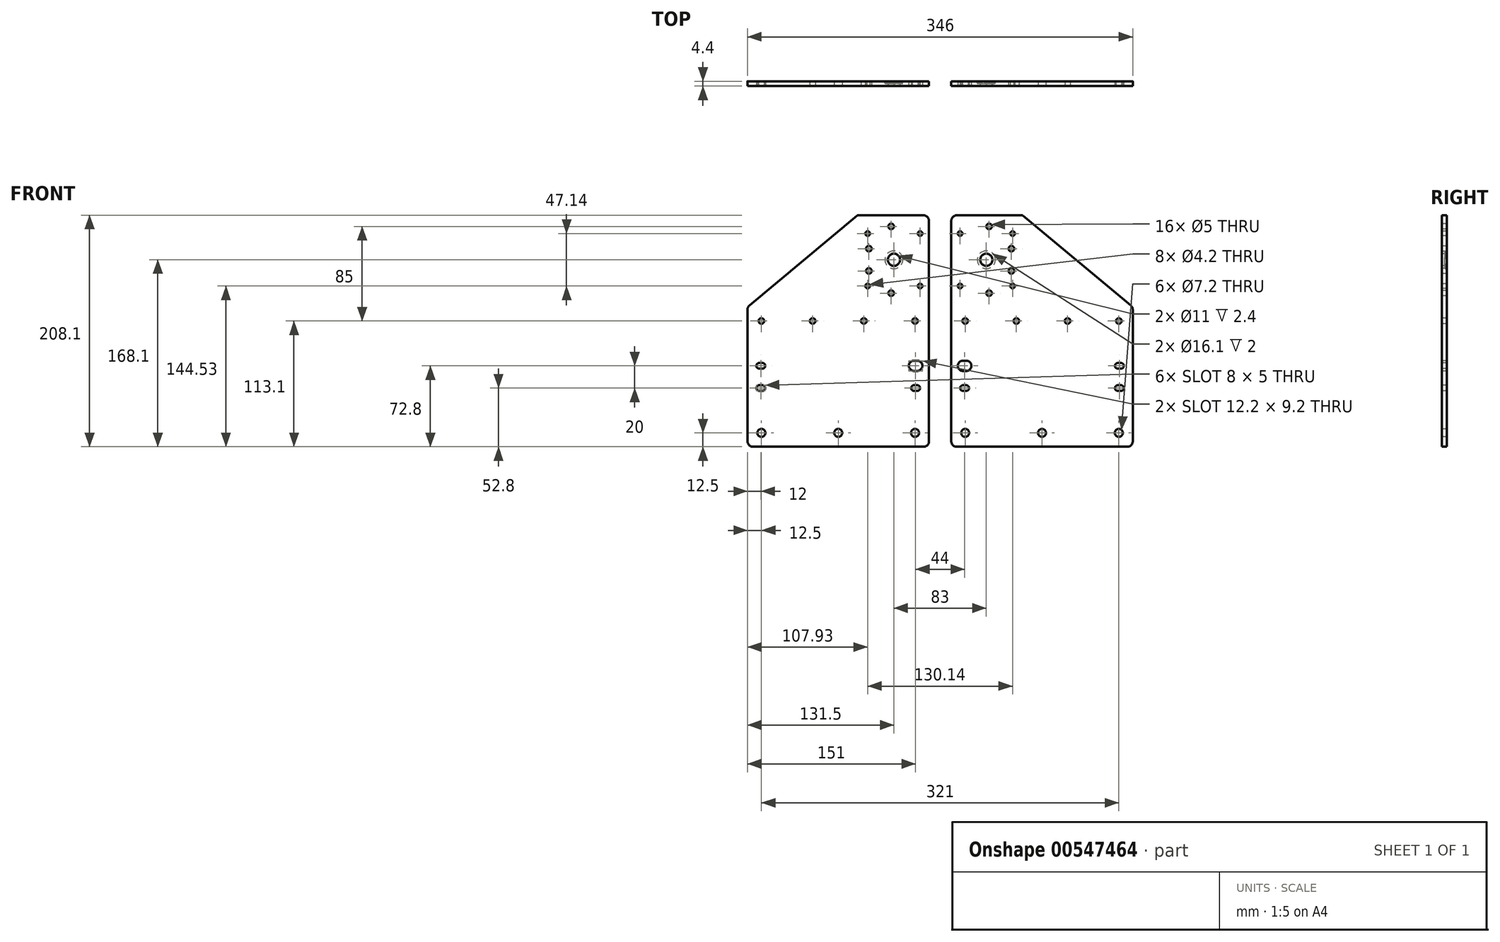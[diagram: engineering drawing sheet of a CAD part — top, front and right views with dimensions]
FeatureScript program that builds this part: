
annotation { "Feature Type Name" : "Feature", "Feature Type Description" : "" }
export const myFeature = defineFeature(function(context is Context, id is Id, definition is map)
    precondition{}
    {
        {
            var Q0;
            Q0=qCreatedBy(makeId("Front.planeOp"),FACE);
            var sketch = newSketch(context, id + "F0", { "sketchPlane" : qUnion([Q0])});
            skCircle(sketch, "E0", {"center": v(-69, -50.3) * mm, "radius": 3.6 * mm});
            skCircle(sketch, "E1", {"center": v(-69, -50.3) * mm, "radius": 6.12 * mm});
            skCircle(sketch, "E2.1.0.0", {"center": v(0, -50.3) * mm, "radius": 6.12 * mm});
            skCircle(sketch, "E2.1.0.1", {"center": v(0, -50.3) * mm, "radius": 3.6 * mm});
            skCircle(sketch, "E2.2.0.0", {"center": v(69, -50.3) * mm, "radius": 6.12 * mm});
            skCircle(sketch, "E2.2.0.1", {"center": v(69, -50.3) * mm, "radius": 3.6 * mm});
            skLineSegment(sketch, "E2.direction1", {"start": v(-69, -50.3) * mm, "end": v(0, -50.3) * mm, "construction": true});
            skArc(sketch, "E3", {"start": v(-68, -12.5) * mm, "mid": v(-65.5, -10) * mm, "end": v(-68, -7.5) * mm});
            skArc(sketch, "E4", {"start": v(-71, -7.5) * mm, "mid": v(-73.5, -10) * mm, "end": v(-71, -12.5) * mm});
            skArc(sketch, "E5", {"start": v(-71, -5.4) * mm, "mid": v(-75.6, -10) * mm, "end": v(-71, -14.6) * mm});
            skArc(sketch, "E6", {"start": v(-68, -14.6) * mm, "mid": v(-63.4, -10) * mm, "end": v(-68, -5.4) * mm});
            skLineSegment(sketch, "E7", {"start": v(-71, -5.4) * mm, "end": v(-68, -5.4) * mm});
            skLineSegment(sketch, "E8", {"start": v(-71, -14.6) * mm, "end": v(-68, -14.6) * mm});
            skLineSegment(sketch, "E9", {"start": v(-71, -12.5) * mm, "end": v(-68, -12.5) * mm});
            skLineSegment(sketch, "E10", {"start": v(-71, -7.5) * mm, "end": v(-68, -7.5) * mm});
            skArc(sketch, "E11.MirrorCS", {"start": v(-71, 5.4) * mm, "mid": v(-75.6, 10) * mm, "end": v(-71, 14.6) * mm});
            skArc(sketch, "E12.MirrorCS", {"start": v(-71, 7.5) * mm, "mid": v(-73.5, 10) * mm, "end": v(-71, 12.5) * mm});
            skArc(sketch, "E13.MirrorCS", {"start": v(-68, 14.6) * mm, "mid": v(-63.4, 10) * mm, "end": v(-68, 5.4) * mm});
            skArc(sketch, "E14.MirrorCS", {"start": v(-68, 12.5) * mm, "mid": v(-65.5, 10) * mm, "end": v(-68, 7.5) * mm});
            skLineSegment(sketch, "E15.MirrorCS", {"start": v(-71, 7.5) * mm, "end": v(-68, 7.5) * mm});
            skLineSegment(sketch, "E16.MirrorCS", {"start": v(-71, 5.4) * mm, "end": v(-68, 5.4) * mm});
            skLineSegment(sketch, "E17.MirrorCS", {"start": v(-71, 12.5) * mm, "end": v(-68, 12.5) * mm});
            skLineSegment(sketch, "E18.MirrorCS", {"start": v(-71, 14.6) * mm, "end": v(-68, 14.6) * mm});
            skLineSegment(sketch, "E19.MirrorCS", {"start": v(71, -12.5) * mm, "end": v(68, -12.5) * mm});
            skLineSegment(sketch, "E20.MirrorCS", {"start": v(71, 7.5) * mm, "end": v(68, 7.5) * mm});
            skLineSegment(sketch, "E21.MirrorCS", {"start": v(71, 14.6) * mm, "end": v(68, 14.6) * mm});
            skLineSegment(sketch, "E22.MirrorCS", {"start": v(71, 12.5) * mm, "end": v(68, 12.5) * mm});
            skLineSegment(sketch, "E23.MirrorCS", {"start": v(71, -5.4) * mm, "end": v(68, -5.4) * mm});
            skLineSegment(sketch, "E24.MirrorCS", {"start": v(71, -14.6) * mm, "end": v(68, -14.6) * mm});
            skLineSegment(sketch, "E25.MirrorCS", {"start": v(71, 5.4) * mm, "end": v(68, 5.4) * mm});
            skLineSegment(sketch, "E26.MirrorCS", {"start": v(71, -7.5) * mm, "end": v(68, -7.5) * mm});
            skArc(sketch, "E27.MirrorCS", {"start": v(71, -7.5) * mm, "mid": v(73.5, -10) * mm, "end": v(71, -12.5) * mm});
            skArc(sketch, "E28.MirrorCS", {"start": v(71, 7.5) * mm, "mid": v(73.5, 10) * mm, "end": v(71, 12.5) * mm});
            skArc(sketch, "E29.MirrorCS", {"start": v(71, 5.4) * mm, "mid": v(75.6, 10) * mm, "end": v(71, 14.6) * mm});
            skArc(sketch, "E30.MirrorCS", {"start": v(68, 14.6) * mm, "mid": v(63.4, 10) * mm, "end": v(68, 5.4) * mm});
            skArc(sketch, "E31.MirrorCS", {"start": v(71, -5.4) * mm, "mid": v(75.6, -10) * mm, "end": v(71, -14.6) * mm});
            skArc(sketch, "E32.MirrorCS", {"start": v(68, -12.5) * mm, "mid": v(65.5, -10) * mm, "end": v(68, -7.5) * mm});
            skArc(sketch, "E33.MirrorCS", {"start": v(68, 12.5) * mm, "mid": v(65.5, 10) * mm, "end": v(68, 7.5) * mm});
            skArc(sketch, "E34.MirrorCS", {"start": v(68, -14.6) * mm, "mid": v(63.4, -10) * mm, "end": v(68, -5.4) * mm});
            skCircle(sketch, "E35", {"center": v(-69, 50.3) * mm, "radius": 2.5 * mm});
            skCircle(sketch, "E36", {"center": v(-69, 50.3) * mm, "radius": 4.6 * mm});
            skCircle(sketch, "E37.1.0.0", {"center": v(-23, 50.3) * mm, "radius": 4.6 * mm});
            skCircle(sketch, "E37.1.0.1", {"center": v(-23, 50.3) * mm, "radius": 2.5 * mm});
            skCircle(sketch, "E37.2.0.0", {"center": v(23, 50.3) * mm, "radius": 4.6 * mm});
            skCircle(sketch, "E37.2.0.1", {"center": v(23, 50.3) * mm, "radius": 2.5 * mm});
            skCircle(sketch, "E37.3.0.0", {"center": v(69, 50.3) * mm, "radius": 4.6 * mm});
            skCircle(sketch, "E37.3.0.1", {"center": v(69, 50.3) * mm, "radius": 2.5 * mm});
            skLineSegment(sketch, "E37.direction1", {"start": v(-69, 50.3) * mm, "end": v(-23, 50.3) * mm, "construction": true});
            skCircle(sketch, "E38", {"center": v(-47.5, 75.3) * mm, "radius": 2.5 * mm});
            skCircle(sketch, "E39", {"center": v(-47.5, 75.3) * mm, "radius": 4.6 * mm});
            skCircle(sketch, "E40", {"center": v(-47.5, 135.3) * mm, "radius": 2.5 * mm});
            skCircle(sketch, "E41", {"center": v(-47.5, 135.3) * mm, "radius": 4.6 * mm});
            skCircle(sketch, "E42", {"center": v(-27.5, 115.3) * mm, "radius": 2.5 * mm});
            skCircle(sketch, "E43", {"center": v(-27.5, 115.3) * mm, "radius": 4.6 * mm});
            skCircle(sketch, "E44", {"center": v(-27.5, 95.3) * mm, "radius": 2.5 * mm});
            skCircle(sketch, "E45", {"center": v(-27.5, 95.3) * mm, "radius": 4.6 * mm});
            skCircle(sketch, "E46", {"center": v(-50, 105.3) * mm, "radius": 5.5 * mm});
            skCircle(sketch, "E47", {"center": v(-73.57, 128.87) * mm, "radius": 2.1 * mm});
            skCircle(sketch, "E48.1.0", {"center": v(-73.57, 81.73) * mm, "radius": 2.1 * mm});
            skCircle(sketch, "E48.2.0", {"center": v(-26.43, 81.73) * mm, "radius": 2.1 * mm});
            skCircle(sketch, "E48.3.0", {"center": v(-26.43, 128.87) * mm, "radius": 2.1 * mm});
            skLineSegment(sketch, "E49.bottom", {"start": v(-57.5, 65.3) * mm, "end": v(-17.5, 65.3) * mm, "construction": true});
            skLineSegment(sketch, "E49.top", {"start": v(-57.5, 145.3) * mm, "end": v(-17.5, 145.3) * mm, "construction": true});
            skLineSegment(sketch, "E49.left", {"start": v(-57.5, 65.3) * mm, "end": v(-57.5, 145.3) * mm, "construction": true});
            skLineSegment(sketch, "E49.right", {"start": v(-17.5, 65.3) * mm, "end": v(-17.5, 145.3) * mm, "construction": true});
            skCircle(sketch, "E50", {"center": v(-69, -50.3) * mm, "radius": 12.5 * mm, "construction": true});
            skCircle(sketch, "E51", {"center": v(69, -50.3) * mm, "radius": 12.5 * mm, "construction": true});
            skCircle(sketch, "E52", {"center": v(69, 50.3) * mm, "radius": 12.5 * mm, "construction": true});
            skLineSegment(sketch, "E53", {"start": v(-76.5, -62.8) * mm, "end": v(76.5, -62.8) * mm});
            skLineSegment(sketch, "E54", {"start": v(81.5, -57.8) * mm, "end": v(81.5, 60.46) * mm});
            skCircle(sketch, "E55", {"center": v(-69, 50.3) * mm, "radius": 12.5 * mm, "construction": true});
            skLineSegment(sketch, "E56", {"start": v(-81.5, -57.8) * mm, "end": v(-81.5, 140.3) * mm});
            skLineSegment(sketch, "E57", {"start": v(-81.5, 62.8) * mm, "end": v(81.5, 62.8) * mm, "construction": true});
            skCircle(sketch, "E58", {"center": v(-47.5, 135.3) * mm, "radius": 10 * mm, "construction": true});
            skLineSegment(sketch, "E59", {"start": v(-76.5, 145.3) * mm, "end": v(-18.04, 145.3) * mm});
            skLineSegment(sketch, "E60", {"start": v(-17.08, 144.95) * mm, "end": v(79.7, 64.3) * mm});
            skPoint(sketch, "E61.visualSharp", {"position": v(-81.5, -62.8) * mm});
            skArc(sketch, "E61.filletArc", {"start": v(-81.5, -57.8) * mm, "mid": v(-80.04, -61.34) * mm, "end": v(-76.5, -62.8) * mm});
            skPoint(sketch, "E62.visualSharp", {"position": v(81.5, -62.8) * mm});
            skArc(sketch, "E62.filletArc", {"start": v(76.5, -62.8) * mm, "mid": v(80.04, -61.34) * mm, "end": v(81.5, -57.8) * mm});
            skPoint(sketch, "E63.visualSharp", {"position": v(-81.5, 145.3) * mm});
            skArc(sketch, "E63.filletArc", {"start": v(-76.5, 145.3) * mm, "mid": v(-80.04, 143.84) * mm, "end": v(-81.5, 140.3) * mm});
            skPoint(sketch, "E64.visualSharp", {"position": v(81.5, 62.8) * mm});
            skArc(sketch, "E64.filletArc", {"start": v(81.5, 60.46) * mm, "mid": v(81.03, 62.58) * mm, "end": v(79.7, 64.3) * mm});
            skPoint(sketch, "E65.visualSharp", {"position": v(-17.5, 145.3) * mm});
            skArc(sketch, "E65.filletArc", {"start": v(-17.08, 144.95) * mm, "mid": v(-17.53, 145.21) * mm, "end": v(-18.04, 145.3) * mm});
            skSolve(sketch);
        }
        {
            var Q0;
            Q0=makeQuery(id+"F0.imprint","IMPRINT",FACE,{"disambiguationData":[TD([[makeQuery(id+"F0.imprint","IMPRINT",EDGE,{"derivedFrom":sQuery(id+"F0.wireOp",EDGE,"E1")}),-1.0]])]});
            var Q1;
            Q1=makeQuery(id+"F0.imprint","IMPRINT",FACE,{"disambiguationData":[TD([[makeQuery(id+"F0.imprint","IMPRINT",EDGE,{"derivedFrom":sQuery(id+"F0.wireOp",EDGE,"E3")}),-1.0]])]});
            var Q2;
            Q2=makeQuery(id+"F0.imprint","IMPRINT",FACE,{"disambiguationData":[TD([[makeQuery(id+"F0.imprint","IMPRINT",EDGE,{"derivedFrom":sQuery(id+"F0.wireOp",EDGE,"E11.MirrorCS")}),-1.0]])]});
            var Q3;
            Q3=makeQuery(id+"F0.imprint","IMPRINT",FACE,{"disambiguationData":[TD([[makeQuery(id+"F0.imprint","IMPRINT",EDGE,{"derivedFrom":sQuery(id+"F0.wireOp",EDGE,"E0")}),-1.0]])]});
            var Q4;
            Q4=makeQuery(id+"F0.imprint","IMPRINT",FACE,{"disambiguationData":[TD([[makeQuery(id+"F0.imprint","IMPRINT",EDGE,{"derivedFrom":sQuery(id+"F0.wireOp",EDGE,"E2.1.0.0")}),1.0]])]});
            var Q5;
            Q5=makeQuery(id+"F0.imprint","IMPRINT",FACE,{"disambiguationData":[TD([[makeQuery(id+"F0.imprint","IMPRINT",EDGE,{"derivedFrom":sQuery(id+"F0.wireOp",EDGE,"E2.2.0.0")}),1.0]])]});
            var Q6;
            Q6=makeQuery(id+"F0.imprint","IMPRINT",FACE,{"disambiguationData":[TD([[makeQuery(id+"F0.imprint","IMPRINT",EDGE,{"derivedFrom":sQuery(id+"F0.wireOp",EDGE,"E19.MirrorCS")}),1.0]])]});
            var Q7;
            Q7=makeQuery(id+"F0.imprint","IMPRINT",FACE,{"disambiguationData":[TD([[makeQuery(id+"F0.imprint","IMPRINT",EDGE,{"derivedFrom":sQuery(id+"F0.wireOp",EDGE,"E20.MirrorCS")}),1.0]])]});
            var Q8;
            Q8=makeQuery(id+"F0.imprint","IMPRINT",FACE,{"disambiguationData":[TD([[makeQuery(id+"F0.imprint","IMPRINT",EDGE,{"derivedFrom":sQuery(id+"F0.wireOp",EDGE,"E37.1.0.0")}),1.0]])]});
            var Q9;
            Q9=makeQuery(id+"F0.imprint","IMPRINT",FACE,{"disambiguationData":[TD([[makeQuery(id+"F0.imprint","IMPRINT",EDGE,{"derivedFrom":sQuery(id+"F0.wireOp",EDGE,"E37.2.0.0")}),1.0]])]});
            var Q10;
            Q10=makeQuery(id+"F0.imprint","IMPRINT",FACE,{"disambiguationData":[TD([[makeQuery(id+"F0.imprint","IMPRINT",EDGE,{"derivedFrom":sQuery(id+"F0.wireOp",EDGE,"E37.3.0.0")}),1.0]])]});
            var Q11;
            Q11=makeQuery(id+"F0.imprint","IMPRINT",FACE,{"disambiguationData":[TD([[makeQuery(id+"F0.imprint","IMPRINT",EDGE,{"derivedFrom":sQuery(id+"F0.wireOp",EDGE,"E35")}),-1.0]])]});
            var Q12;
            Q12=makeQuery(id+"F0.imprint","IMPRINT",FACE,{"disambiguationData":[TD([[makeQuery(id+"F0.imprint","IMPRINT",EDGE,{"derivedFrom":sQuery(id+"F0.wireOp",EDGE,"E38")}),-1.0]])]});
            var Q13;
            Q13=makeQuery(id+"F0.imprint","IMPRINT",FACE,{"disambiguationData":[TD([[makeQuery(id+"F0.imprint","IMPRINT",EDGE,{"derivedFrom":sQuery(id+"F0.wireOp",EDGE,"E44")}),-1.0]])]});
            var Q14;
            Q14=makeQuery(id+"F0.imprint","IMPRINT",FACE,{"disambiguationData":[TD([[makeQuery(id+"F0.imprint","IMPRINT",EDGE,{"derivedFrom":sQuery(id+"F0.wireOp",EDGE,"E42")}),-1.0]])]});
            var Q15;
            Q15=makeQuery(id+"F0.imprint","IMPRINT",FACE,{"disambiguationData":[TD([[makeQuery(id+"F0.imprint","IMPRINT",EDGE,{"derivedFrom":sQuery(id+"F0.wireOp",EDGE,"E40")}),-1.0]])]});
            extrude(context, id + "F1", {"entities" : qUnion([Q0, Q1, Q2, Q3, Q4, Q5, Q6, Q7, Q8, Q9, Q10, Q11, Q12, Q13, Q14, Q15]), "oppositeDirection" : true, "depth" : 6 * mm, "offsetDistance" : 25 * mm});
        }
        {
            var Q0;
            Q0=makeQuery(id+"F0.imprint","IMPRINT",FACE,{"disambiguationData":[TD([[makeQuery(id+"F0.imprint","IMPRINT",EDGE,{"derivedFrom":sQuery(id+"F0.wireOp",EDGE,"E40")}),-1.0]])]});
            var Q1;
            Q1=makeQuery(id+"F0.imprint","IMPRINT",FACE,{"disambiguationData":[TD([[makeQuery(id+"F0.imprint","IMPRINT",EDGE,{"derivedFrom":sQuery(id+"F0.wireOp",EDGE,"E42")}),-1.0]])]});
            var Q2;
            Q2=makeQuery(id+"F0.imprint","IMPRINT",FACE,{"disambiguationData":[TD([[makeQuery(id+"F0.imprint","IMPRINT",EDGE,{"derivedFrom":sQuery(id+"F0.wireOp",EDGE,"E38")}),-1.0]])]});
            var Q3;
            Q3=makeQuery(id+"F0.imprint","IMPRINT",FACE,{"disambiguationData":[TD([[makeQuery(id+"F0.imprint","IMPRINT",EDGE,{"derivedFrom":sQuery(id+"F0.wireOp",EDGE,"E44")}),-1.0]])]});
            var Q4;
            Q4=makeQuery(id+"F0.imprint","IMPRINT",FACE,{"disambiguationData":[TD([[makeQuery(id+"F0.imprint","IMPRINT",EDGE,{"derivedFrom":sQuery(id+"F0.wireOp",EDGE,"E11.MirrorCS")}),-1.0]])]});
            var Q5;
            Q5=makeQuery(id+"F0.imprint","IMPRINT",FACE,{"disambiguationData":[TD([[makeQuery(id+"F0.imprint","IMPRINT",EDGE,{"derivedFrom":sQuery(id+"F0.wireOp",EDGE,"E3")}),-1.0]])]});
            var Q6;
            Q6=makeQuery(id+"F0.imprint","IMPRINT",FACE,{"disambiguationData":[TD([[makeQuery(id+"F0.imprint","IMPRINT",EDGE,{"derivedFrom":sQuery(id+"F0.wireOp",EDGE,"E35")}),-1.0]])]});
            var Q7;
            Q7=makeQuery(id+"F0.imprint","IMPRINT",FACE,{"disambiguationData":[TD([[makeQuery(id+"F0.imprint","IMPRINT",EDGE,{"derivedFrom":sQuery(id+"F0.wireOp",EDGE,"E37.1.0.0")}),1.0]])]});
            var Q8;
            Q8=makeQuery(id+"F0.imprint","IMPRINT",FACE,{"disambiguationData":[TD([[makeQuery(id+"F0.imprint","IMPRINT",EDGE,{"derivedFrom":sQuery(id+"F0.wireOp",EDGE,"E37.2.0.0")}),1.0]])]});
            var Q9;
            Q9=makeQuery(id+"F0.imprint","IMPRINT",FACE,{"disambiguationData":[TD([[makeQuery(id+"F0.imprint","IMPRINT",EDGE,{"derivedFrom":sQuery(id+"F0.wireOp",EDGE,"E37.3.0.0")}),1.0]])]});
            var Q10;
            Q10=makeQuery(id+"F0.imprint","IMPRINT",FACE,{"disambiguationData":[TD([[makeQuery(id+"F0.imprint","IMPRINT",EDGE,{"derivedFrom":sQuery(id+"F0.wireOp",EDGE,"E20.MirrorCS")}),1.0]])]});
            var Q11;
            Q11=makeQuery(id+"F0.imprint","IMPRINT",FACE,{"disambiguationData":[TD([[makeQuery(id+"F0.imprint","IMPRINT",EDGE,{"derivedFrom":sQuery(id+"F0.wireOp",EDGE,"E19.MirrorCS")}),1.0]])]});
            var Q12;
            Q12=makeQuery(id+"F0.imprint","IMPRINT",FACE,{"disambiguationData":[TD([[makeQuery(id+"F0.imprint","IMPRINT",EDGE,{"derivedFrom":sQuery(id+"F0.wireOp",EDGE,"E2.2.0.0")}),1.0]])]});
            var Q13;
            Q13=makeQuery(id+"F0.imprint","IMPRINT",FACE,{"disambiguationData":[TD([[makeQuery(id+"F0.imprint","IMPRINT",EDGE,{"derivedFrom":sQuery(id+"F0.wireOp",EDGE,"E2.1.0.0")}),1.0]])]});
            var Q14;
            Q14=makeQuery(id+"F0.imprint","IMPRINT",FACE,{"disambiguationData":[TD([[makeQuery(id+"F0.imprint","IMPRINT",EDGE,{"derivedFrom":sQuery(id+"F0.wireOp",EDGE,"E0")}),-1.0]])]});
            extrude(context, id + "F2", {"entities" : qUnion([Q0, Q1, Q2, Q3, Q4, Q5, Q6, Q7, Q8, Q9, Q10, Q11, Q12, Q13, Q14]), "operationType" : NewBodyOperationType.REMOVE, "oppositeDirection" : true, "depth" : 1.6 * mm, "offsetDistance" : 25 * mm});
        }
        {
            var Q0;
            Q0=makeQuery(id+"F1.opExtrude","CAP_FACE",FACE,{"disambiguationData":[OSD([sQuery(id+"F0.wireOp",EDGE,"E0"),sQuery(id+"F0.wireOp",EDGE,"E2.1.0.1"),sQuery(id+"F0.wireOp",EDGE,"E2.2.0.1"),sQuery(id+"F0.wireOp",EDGE,"E3"),sQuery(id+"F0.wireOp",EDGE,"E4"),sQuery(id+"F0.wireOp",EDGE,"E9"),sQuery(id+"F0.wireOp",EDGE,"E10"),sQuery(id+"F0.wireOp",EDGE,"E12.MirrorCS"),sQuery(id+"F0.wireOp",EDGE,"E14.MirrorCS"),sQuery(id+"F0.wireOp",EDGE,"E15.MirrorCS"),sQuery(id+"F0.wireOp",EDGE,"E17.MirrorCS"),sQuery(id+"F0.wireOp",EDGE,"E19.MirrorCS"),sQuery(id+"F0.wireOp",EDGE,"E20.MirrorCS"),sQuery(id+"F0.wireOp",EDGE,"E22.MirrorCS"),sQuery(id+"F0.wireOp",EDGE,"E26.MirrorCS"),sQuery(id+"F0.wireOp",EDGE,"E27.MirrorCS"),sQuery(id+"F0.wireOp",EDGE,"E28.MirrorCS"),sQuery(id+"F0.wireOp",EDGE,"E32.MirrorCS"),sQuery(id+"F0.wireOp",EDGE,"E33.MirrorCS"),sQuery(id+"F0.wireOp",EDGE,"E35"),sQuery(id+"F0.wireOp",EDGE,"E37.1.0.1"),sQuery(id+"F0.wireOp",EDGE,"E37.2.0.1"),sQuery(id+"F0.wireOp",EDGE,"E37.3.0.1"),sQuery(id+"F0.wireOp",EDGE,"E38"),sQuery(id+"F0.wireOp",EDGE,"E40"),sQuery(id+"F0.wireOp",EDGE,"E42"),sQuery(id+"F0.wireOp",EDGE,"E44"),sQuery(id+"F0.wireOp",EDGE,"E46"),sQuery(id+"F0.wireOp",EDGE,"E47"),sQuery(id+"F0.wireOp",EDGE,"E48.1.0"),sQuery(id+"F0.wireOp",EDGE,"E48.2.0"),sQuery(id+"F0.wireOp",EDGE,"E48.3.0"),sQuery(id+"F0.wireOp",EDGE,"E53"),sQuery(id+"F0.wireOp",EDGE,"E54"),sQuery(id+"F0.wireOp",EDGE,"E56"),sQuery(id+"F0.wireOp",EDGE,"E59"),sQuery(id+"F0.wireOp",EDGE,"E60"),sQuery(id+"F0.wireOp",EDGE,"E61.filletArc"),sQuery(id+"F0.wireOp",EDGE,"E62.filletArc"),sQuery(id+"F0.wireOp",EDGE,"E63.filletArc"),sQuery(id+"F0.wireOp",EDGE,"E64.filletArc"),sQuery(id+"F0.wireOp",EDGE,"E65.filletArc")])],"isStart":false});
            var sketch = newSketch(context, id + "F3", { "sketchPlane" : qUnion([Q0])});
            skCircle(sketch, "E66", {"center": v(50, 105.3) * mm, "radius": 8.05 * mm});
            skSolve(sketch);
        }
        {
            var Q0;
            Q0=makeQuery(id+"F3.imprint","IMPRINT",FACE,{"disambiguationData":[TD([[makeQuery(id+"F3.imprint","IMPRINT",EDGE,{"derivedFrom":sQuery(id+"F3.wireOp",EDGE,"E66")}),1.0]])]});
            extrude(context, id + "F4", {"entities" : qUnion([Q0]), "operationType" : NewBodyOperationType.REMOVE, "oppositeDirection" : true, "depth" : 2 * mm, "offsetDistance" : 25 * mm});
        }
        {
            var Q0;
            Q0=makeQuery(id+"F1.opExtrude","SWEPT_BODY",BODY,{"disambiguationData":[OSD([sQuery(id+"F0.wireOp",EDGE,"E0"),sQuery(id+"F0.wireOp",EDGE,"E2.1.0.1"),sQuery(id+"F0.wireOp",EDGE,"E2.2.0.1"),sQuery(id+"F0.wireOp",EDGE,"E3"),sQuery(id+"F0.wireOp",EDGE,"E4"),sQuery(id+"F0.wireOp",EDGE,"E9"),sQuery(id+"F0.wireOp",EDGE,"E10"),sQuery(id+"F0.wireOp",EDGE,"E12.MirrorCS"),sQuery(id+"F0.wireOp",EDGE,"E14.MirrorCS"),sQuery(id+"F0.wireOp",EDGE,"E15.MirrorCS"),sQuery(id+"F0.wireOp",EDGE,"E17.MirrorCS"),sQuery(id+"F0.wireOp",EDGE,"E19.MirrorCS"),sQuery(id+"F0.wireOp",EDGE,"E20.MirrorCS"),sQuery(id+"F0.wireOp",EDGE,"E22.MirrorCS"),sQuery(id+"F0.wireOp",EDGE,"E26.MirrorCS"),sQuery(id+"F0.wireOp",EDGE,"E27.MirrorCS"),sQuery(id+"F0.wireOp",EDGE,"E28.MirrorCS"),sQuery(id+"F0.wireOp",EDGE,"E32.MirrorCS"),sQuery(id+"F0.wireOp",EDGE,"E33.MirrorCS"),sQuery(id+"F0.wireOp",EDGE,"E35"),sQuery(id+"F0.wireOp",EDGE,"E37.1.0.1"),sQuery(id+"F0.wireOp",EDGE,"E37.2.0.1"),sQuery(id+"F0.wireOp",EDGE,"E37.3.0.1"),sQuery(id+"F0.wireOp",EDGE,"E38"),sQuery(id+"F0.wireOp",EDGE,"E40"),sQuery(id+"F0.wireOp",EDGE,"E42"),sQuery(id+"F0.wireOp",EDGE,"E44"),sQuery(id+"F0.wireOp",EDGE,"E46"),sQuery(id+"F0.wireOp",EDGE,"E47"),sQuery(id+"F0.wireOp",EDGE,"E48.1.0"),sQuery(id+"F0.wireOp",EDGE,"E48.2.0"),sQuery(id+"F0.wireOp",EDGE,"E48.3.0"),sQuery(id+"F0.wireOp",EDGE,"E53"),sQuery(id+"F0.wireOp",EDGE,"E54"),sQuery(id+"F0.wireOp",EDGE,"E56"),sQuery(id+"F0.wireOp",EDGE,"E59"),sQuery(id+"F0.wireOp",EDGE,"E60"),sQuery(id+"F0.wireOp",EDGE,"E61.filletArc"),sQuery(id+"F0.wireOp",EDGE,"E62.filletArc"),sQuery(id+"F0.wireOp",EDGE,"E63.filletArc"),sQuery(id+"F0.wireOp",EDGE,"E64.filletArc"),sQuery(id+"F0.wireOp",EDGE,"E65.filletArc")])]});
            var Q1;
            Q1=makeQuery(id+"F1.opExtrude","SWEPT_FACE",FACE,{"disambiguationData":[OSD([sQuery(id+"F0.wireOp",EDGE,"E56")])]});
            mirror(context, id + "F5", {"entities" : qUnion([Q0]), "mirrorPlane" : qUnion([Q1])});
        }
        {
            var Q0;
            Q0=makeQuery(id+"F5.opPattern","COPY",BODY,{"derivedFrom":makeQuery(id+"F1.opExtrude","SWEPT_BODY",BODY,{"disambiguationData":[OSD([sQuery(id+"F0.wireOp",EDGE,"E0"),sQuery(id+"F0.wireOp",EDGE,"E2.1.0.1"),sQuery(id+"F0.wireOp",EDGE,"E2.2.0.1"),sQuery(id+"F0.wireOp",EDGE,"E3"),sQuery(id+"F0.wireOp",EDGE,"E4"),sQuery(id+"F0.wireOp",EDGE,"E9"),sQuery(id+"F0.wireOp",EDGE,"E10"),sQuery(id+"F0.wireOp",EDGE,"E12.MirrorCS"),sQuery(id+"F0.wireOp",EDGE,"E14.MirrorCS"),sQuery(id+"F0.wireOp",EDGE,"E15.MirrorCS"),sQuery(id+"F0.wireOp",EDGE,"E17.MirrorCS"),sQuery(id+"F0.wireOp",EDGE,"E19.MirrorCS"),sQuery(id+"F0.wireOp",EDGE,"E20.MirrorCS"),sQuery(id+"F0.wireOp",EDGE,"E22.MirrorCS"),sQuery(id+"F0.wireOp",EDGE,"E26.MirrorCS"),sQuery(id+"F0.wireOp",EDGE,"E27.MirrorCS"),sQuery(id+"F0.wireOp",EDGE,"E28.MirrorCS"),sQuery(id+"F0.wireOp",EDGE,"E32.MirrorCS"),sQuery(id+"F0.wireOp",EDGE,"E33.MirrorCS"),sQuery(id+"F0.wireOp",EDGE,"E35"),sQuery(id+"F0.wireOp",EDGE,"E37.1.0.1"),sQuery(id+"F0.wireOp",EDGE,"E37.2.0.1"),sQuery(id+"F0.wireOp",EDGE,"E37.3.0.1"),sQuery(id+"F0.wireOp",EDGE,"E38"),sQuery(id+"F0.wireOp",EDGE,"E40"),sQuery(id+"F0.wireOp",EDGE,"E42"),sQuery(id+"F0.wireOp",EDGE,"E44"),sQuery(id+"F0.wireOp",EDGE,"E46"),sQuery(id+"F0.wireOp",EDGE,"E47"),sQuery(id+"F0.wireOp",EDGE,"E48.1.0"),sQuery(id+"F0.wireOp",EDGE,"E48.2.0"),sQuery(id+"F0.wireOp",EDGE,"E48.3.0"),sQuery(id+"F0.wireOp",EDGE,"E53"),sQuery(id+"F0.wireOp",EDGE,"E54"),sQuery(id+"F0.wireOp",EDGE,"E56"),sQuery(id+"F0.wireOp",EDGE,"E59"),sQuery(id+"F0.wireOp",EDGE,"E60"),sQuery(id+"F0.wireOp",EDGE,"E61.filletArc"),sQuery(id+"F0.wireOp",EDGE,"E62.filletArc"),sQuery(id+"F0.wireOp",EDGE,"E63.filletArc"),sQuery(id+"F0.wireOp",EDGE,"E64.filletArc"),sQuery(id+"F0.wireOp",EDGE,"E65.filletArc")])]}),"instanceName":"1"});
            transform(context, id + "F6", {"entities" : qUnion([Q0]), "transformType" : TransformType.TRANSLATION_3D, "dx" : -20 * mm, "dy" : 0 * mm, "dz" : 0 * mm, "makeCopy" : false});
        }
    });
